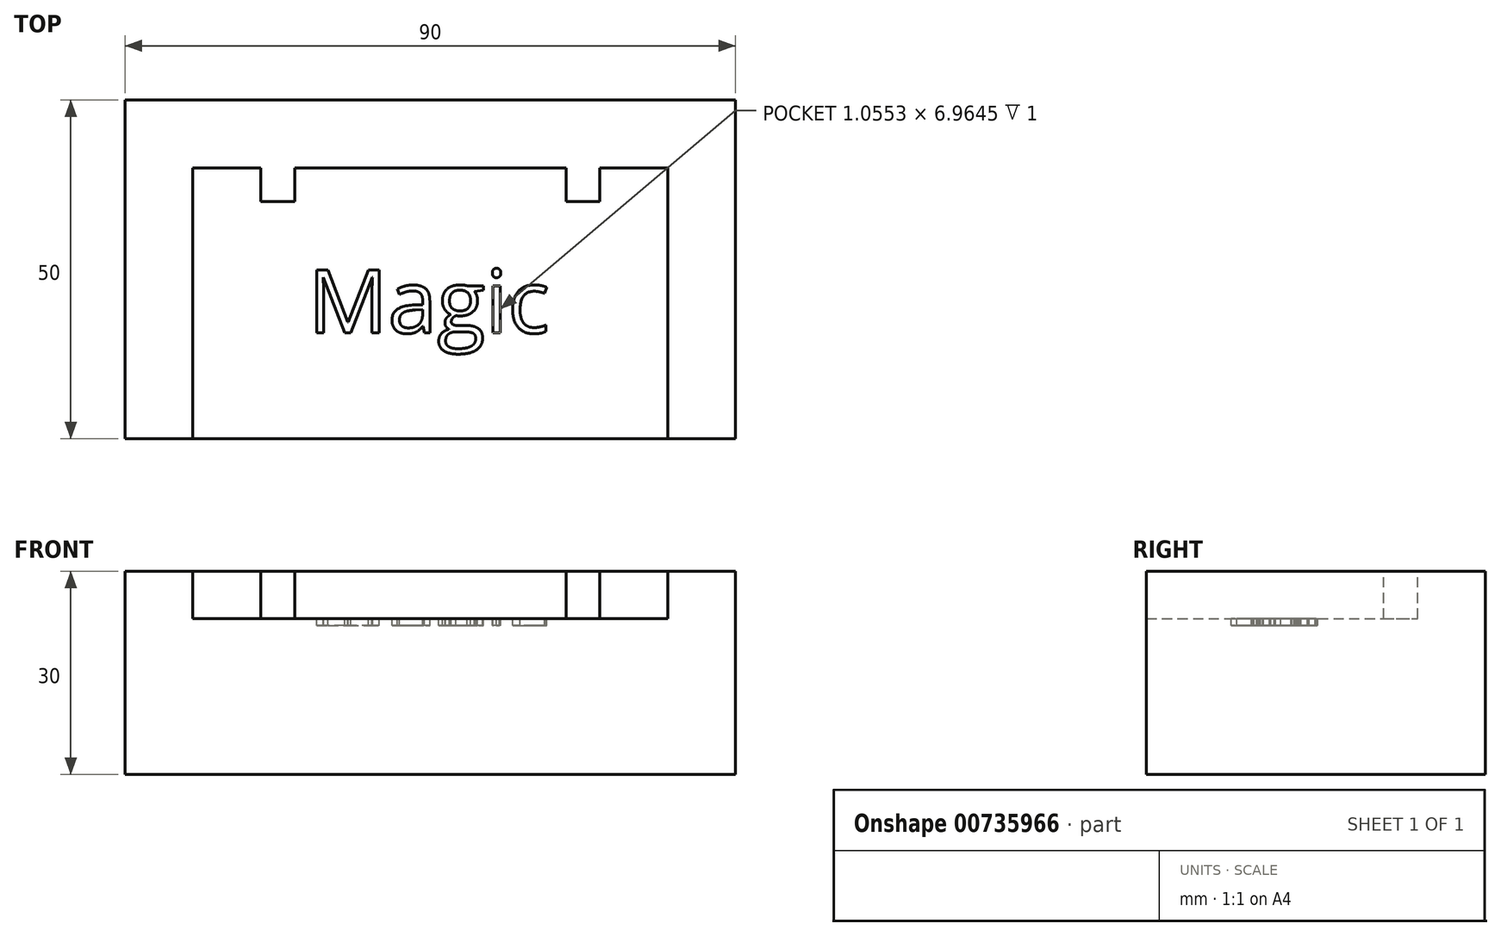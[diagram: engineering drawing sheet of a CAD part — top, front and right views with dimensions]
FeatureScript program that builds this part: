
annotation { "Feature Type Name" : "Feature", "Feature Type Description" : "" }
export const myFeature = defineFeature(function(context is Context, id is Id, definition is map)
    precondition{}
    {
        {
            var Q0;
            Q0=qCreatedBy(makeId("Top.planeOp"),FACE);
            var sketch = newSketch(context, id + "F0", { "sketchPlane" : qUnion([Q0])});
            skLineSegment(sketch, "E0.bottom", {"start": v(-43.65, 24.23) * mm, "end": v(46.35, 24.23) * mm});
            skLineSegment(sketch, "E0.top", {"start": v(-43.65, -25.77) * mm, "end": v(46.35, -25.77) * mm});
            skLineSegment(sketch, "E0.left", {"start": v(-43.65, 24.23) * mm, "end": v(-43.65, -25.77) * mm});
            skLineSegment(sketch, "E0.right", {"start": v(46.35, 24.23) * mm, "end": v(46.35, -25.77) * mm});
            skSolve(sketch);
        }
        {
            var Q0;
            Q0=makeQuery(id+"F0.imprint","IMPRINT",FACE,{"disambiguationData":[TD([[makeQuery(id+"F0.imprint","IMPRINT",EDGE,{"derivedFrom":sQuery(id+"F0.wireOp",EDGE,"E0.bottom")}),-1.0]])]});
            extrude(context, id + "F1", {"entities" : qUnion([Q0]), "depth" : 30 * mm, "offsetDistance" : 25 * mm});
        }
        {
            var Q0;
            Q0=makeQuery(id+"F1.opExtrude","CAP_FACE",FACE,{"disambiguationData":[OSD([sQuery(id+"F0.wireOp",EDGE,"E0.bottom"),sQuery(id+"F0.wireOp",EDGE,"E0.top"),sQuery(id+"F0.wireOp",EDGE,"E0.left"),sQuery(id+"F0.wireOp",EDGE,"E0.right")])],"isStart":false});
            var sketch = newSketch(context, id + "F2", { "sketchPlane" : qUnion([Q0])});
            skLineSegment(sketch, "E1.bottom", {"start": v(-33.65, -25.77) * mm, "end": v(36.35, -25.77) * mm});
            skLineSegment(sketch, "E1.top", {"start": v(-33.65, 14.23) * mm, "end": v(36.35, 14.23) * mm});
            skLineSegment(sketch, "E1.left", {"start": v(-33.65, -25.77) * mm, "end": v(-33.65, 14.23) * mm});
            skLineSegment(sketch, "E1.right", {"start": v(36.35, -25.77) * mm, "end": v(36.35, 14.23) * mm});
            skSolve(sketch);
        }
        {
            var Q0;
            Q0=makeQuery(id+"F2.imprint","IMPRINT",FACE,{"disambiguationData":[TD([[makeQuery(id+"F2.imprint","IMPRINT",EDGE,{"derivedFrom":sQuery(id+"F2.wireOp",EDGE,"E1.bottom")}),1.0]])]});
            extrude(context, id + "F3", {"entities" : qUnion([Q0]), "operationType" : NewBodyOperationType.REMOVE, "oppositeDirection" : true, "depth" : 7 * mm, "offsetDistance" : 25 * mm});
        }
        {
            var Q0;
            Q0=makeQuery(id+"F3.boolean.opBoolean","COPY",FACE,{"derivedFrom":makeQuery(id+"F3.opExtrude","CAP_FACE",FACE,{"disambiguationData":[OSD([sQuery(id+"F2.wireOp",EDGE,"E1.bottom"),sQuery(id+"F2.wireOp",EDGE,"E1.top"),sQuery(id+"F2.wireOp",EDGE,"E1.left"),sQuery(id+"F2.wireOp",EDGE,"E1.right")])],"isStart":false})});
            var sketch = newSketch(context, id + "F4", { "sketchPlane" : qUnion([Q0])});
            skText(sketch, "E2", { "text": "Magic\n", "fontName": "OpenSans-Regular.ttf"});
            const initialGuessF4  = {"E2": [-0.01665, -0.01014, 1, 0, 0.00937]};
            skSetInitialGuess(sketch, initialGuessF4);
            skSolve(sketch);
        }
        {
            var Q0;
            Q0 = qSketchRegion(id + "F4", true);
            extrude(context, id + "F5", {"entities" : qUnion([Q0]), "operationType" : NewBodyOperationType.REMOVE, "oppositeDirection" : true, "depth" : 1 * mm, "offsetDistance" : 25 * mm});
        }
        {
            var Q0;
            Q0=makeQuery(id+"F3.boolean.opBoolean","COPY",FACE,{"derivedFrom":makeQuery(id+"F3.opExtrude","SWEPT_FACE",FACE,{"disambiguationData":[OSD([sQuery(id+"F2.wireOp",EDGE,"E1.top")])]})});
            var sketch = newSketch(context, id + "F6", { "sketchPlane" : qUnion([Q0])});
            skLineSegment(sketch, "E3.bottom", {"start": v(-23.65, 23) * mm, "end": v(-18.65, 23) * mm});
            skLineSegment(sketch, "E3.top", {"start": v(-23.65, 30) * mm, "end": v(-18.65, 30) * mm});
            skLineSegment(sketch, "E3.left", {"start": v(-23.65, 23) * mm, "end": v(-23.65, 30) * mm});
            skLineSegment(sketch, "E3.right", {"start": v(-18.65, 23) * mm, "end": v(-18.65, 30) * mm});
            skLineSegment(sketch, "E4.bottom", {"start": v(26.35, 23) * mm, "end": v(21.35, 23) * mm});
            skLineSegment(sketch, "E4.top", {"start": v(26.35, 30) * mm, "end": v(21.35, 30) * mm});
            skLineSegment(sketch, "E4.left", {"start": v(26.35, 23) * mm, "end": v(26.35, 30) * mm});
            skLineSegment(sketch, "E4.right", {"start": v(21.35, 23) * mm, "end": v(21.35, 30) * mm});
            skSolve(sketch);
        }
        {
            var Q0;
            Q0=makeQuery(id+"F6.imprint","IMPRINT",FACE,{"disambiguationData":[TD([[makeQuery(id+"F6.imprint","IMPRINT",EDGE,{"derivedFrom":sQuery(id+"F6.wireOp",EDGE,"E3.bottom")}),1.0]])]});
            var Q1;
            Q1=makeQuery(id+"F6.imprint","IMPRINT",FACE,{"disambiguationData":[TD([[makeQuery(id+"F6.imprint","IMPRINT",EDGE,{"derivedFrom":sQuery(id+"F6.wireOp",EDGE,"E4.bottom")}),1.0]])]});
            extrude(context, id + "F7", {"entities" : qUnion([Q0, Q1]), "operationType" : NewBodyOperationType.ADD, "depth" : 5 * mm, "offsetDistance" : 25 * mm});
        }
    });
